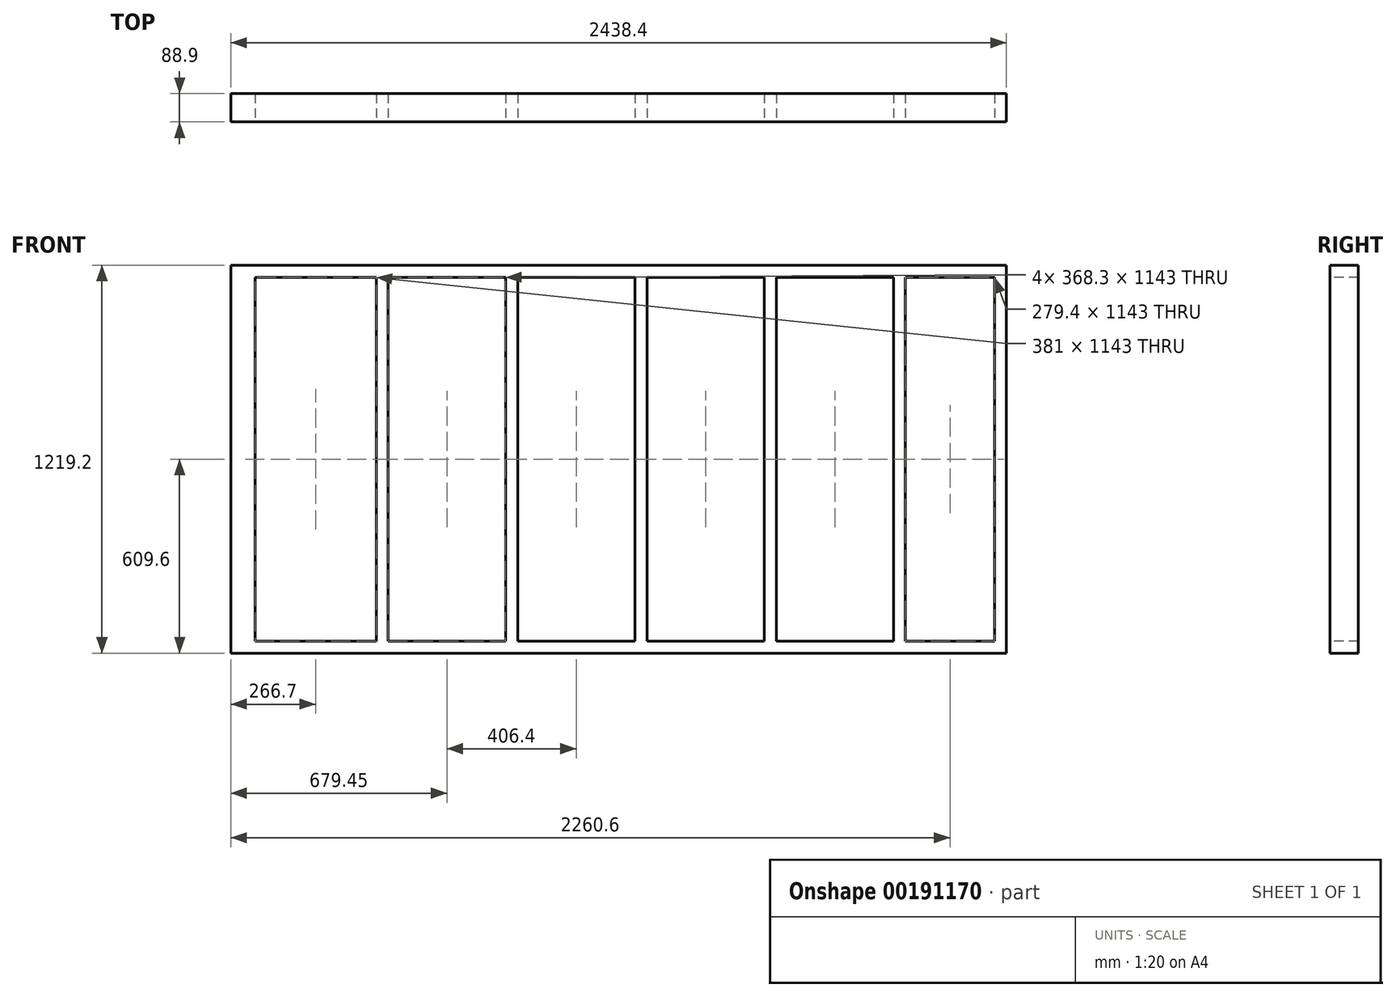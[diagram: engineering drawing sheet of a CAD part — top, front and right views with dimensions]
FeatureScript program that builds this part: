
annotation { "Feature Type Name" : "Feature", "Feature Type Description" : "" }
export const myFeature = defineFeature(function(context is Context, id is Id, definition is map)
    precondition{}
    {
        {
            var Q0;
            Q0=qCreatedBy(makeId("Top.planeOp"),FACE);
            var sketch = newSketch(context, id + "F0", { "sketchPlane" : qUnion([Q0])});
            skLineSegment(sketch, "E0.bottom", {"start": v(1219.2, -44.45) * mm, "end": v(-1219.2, -44.45) * mm});
            skLineSegment(sketch, "E0.top", {"start": v(1219.2, 44.45) * mm, "end": v(-1219.2, 44.45) * mm});
            skLineSegment(sketch, "E0.left", {"start": v(1219.2, -44.45) * mm, "end": v(1219.2, 44.45) * mm});
            skLineSegment(sketch, "E0.right", {"start": v(-1219.2, -44.45) * mm, "end": v(-1219.2, 44.45) * mm});
            skPoint(sketch, "E0.middle", {"position": v(0, 0) * mm});
            skSolve(sketch);
        }
        {
            var Q0;
            Q0 = qSketchRegion(id + "F0", true);
            extrude(context, id + "F1", {"entities" : qUnion([Q0]), "depth" : 38.1 * mm});
        }
        {
            var Q0;
            Q0=makeQuery(id+"F1.opExtrude","CAP_FACE",FACE,{"disambiguationData":[OSD([sQuery(id+"F0.wireOp",EDGE,"E0.bottom"),sQuery(id+"F0.wireOp",EDGE,"E0.top"),sQuery(id+"F0.wireOp",EDGE,"E0.left"),sQuery(id+"F0.wireOp",EDGE,"E0.right")])],"isStart":false});
            var sketch = newSketch(context, id + "F2", { "sketchPlane" : qUnion([Q0])});
            skLineSegment(sketch, "E1.bottom", {"start": v(1219.2, 44.45) * mm, "end": v(1181.1, 44.45) * mm});
            skLineSegment(sketch, "E1.top", {"start": v(1219.2, -44.45) * mm, "end": v(1181.1, -44.45) * mm});
            skLineSegment(sketch, "E1.left", {"start": v(1219.2, 44.45) * mm, "end": v(1219.2, -44.45) * mm});
            skLineSegment(sketch, "E1.right", {"start": v(1181.1, 44.45) * mm, "end": v(1181.1, -44.45) * mm});
            skLineSegment(sketch, "E2.bottom", {"start": v(901.7, 44.45) * mm, "end": v(863.6, 44.45) * mm});
            skLineSegment(sketch, "E2.top", {"start": v(901.7, -44.45) * mm, "end": v(863.6, -44.45) * mm});
            skLineSegment(sketch, "E2.left", {"start": v(901.7, 44.45) * mm, "end": v(901.7, -44.45) * mm});
            skLineSegment(sketch, "E2.right", {"start": v(863.6, 44.45) * mm, "end": v(863.6, -44.45) * mm});
            skLineSegment(sketch, "E3.bottom", {"start": v(495.3, 44.45) * mm, "end": v(457.2, 44.45) * mm});
            skLineSegment(sketch, "E3.top", {"start": v(495.3, -44.45) * mm, "end": v(457.2, -44.45) * mm});
            skLineSegment(sketch, "E3.left", {"start": v(495.3, 44.45) * mm, "end": v(495.3, -44.45) * mm});
            skLineSegment(sketch, "E3.right", {"start": v(457.2, 44.45) * mm, "end": v(457.2, -44.45) * mm});
            skLineSegment(sketch, "E4.bottom", {"start": v(88.9, 44.45) * mm, "end": v(50.8, 44.45) * mm});
            skLineSegment(sketch, "E4.top", {"start": v(88.9, -44.45) * mm, "end": v(50.8, -44.45) * mm});
            skLineSegment(sketch, "E4.left", {"start": v(88.9, 44.45) * mm, "end": v(88.9, -44.45) * mm});
            skLineSegment(sketch, "E4.right", {"start": v(50.8, 44.45) * mm, "end": v(50.8, -44.45) * mm});
            skLineSegment(sketch, "E5.bottom", {"start": v(-317.5, 44.45) * mm, "end": v(-355.6, 44.45) * mm});
            skLineSegment(sketch, "E5.top", {"start": v(-317.5, -44.45) * mm, "end": v(-355.6, -44.45) * mm});
            skLineSegment(sketch, "E5.left", {"start": v(-317.5, 44.45) * mm, "end": v(-317.5, -44.45) * mm});
            skLineSegment(sketch, "E5.right", {"start": v(-355.6, 44.45) * mm, "end": v(-355.6, -44.45) * mm});
            skLineSegment(sketch, "E6.bottom", {"start": v(-723.9, 44.45) * mm, "end": v(-762, 44.45) * mm});
            skLineSegment(sketch, "E6.top", {"start": v(-723.9, -44.45) * mm, "end": v(-762, -44.45) * mm});
            skLineSegment(sketch, "E6.left", {"start": v(-723.9, 44.45) * mm, "end": v(-723.9, -44.45) * mm});
            skLineSegment(sketch, "E6.right", {"start": v(-762, 44.45) * mm, "end": v(-762, -44.45) * mm});
            skLineSegment(sketch, "E7.bottom", {"start": v(-1219.2, 44.45) * mm, "end": v(-1181.1, 44.45) * mm});
            skLineSegment(sketch, "E7.top", {"start": v(-1219.2, -44.45) * mm, "end": v(-1181.1, -44.45) * mm});
            skLineSegment(sketch, "E7.left", {"start": v(-1219.2, 44.45) * mm, "end": v(-1219.2, -44.45) * mm});
            skLineSegment(sketch, "E7.right", {"start": v(-1181.1, 44.45) * mm, "end": v(-1181.1, -44.45) * mm});
            skLineSegment(sketch, "E8.bottom", {"start": v(-1181.1, 44.45) * mm, "end": v(-1143, 44.45) * mm});
            skLineSegment(sketch, "E8.top", {"start": v(-1181.1, -44.45) * mm, "end": v(-1143, -44.45) * mm});
            skLineSegment(sketch, "E8.right", {"start": v(-1143, 44.45) * mm, "end": v(-1143, -44.45) * mm});
            skSolve(sketch);
        }
        {
            var Q0;
            Q0 = qSketchRegion(id + "F2", true);
            extrude(context, id + "F3", {"entities" : qUnion([Q0]), "operationType" : NewBodyOperationType.ADD, "depth" : 1143 * mm});
        }
        {
            var Q0;
            Q0=makeQuery(id+"F3.boolean.opBoolean","MERGE",FACE,{"derivedFrom":[makeQuery(id+"F1.opExtrude","SWEPT_FACE",FACE,{"disambiguationData":[OSD([sQuery(id+"F0.wireOp",EDGE,"E0.bottom")])]}),makeQuery(id+"F3.opExtrude","SWEPT_FACE",FACE,{"disambiguationData":[OSD([sQuery(id+"F2.wireOp",EDGE,"E1.top")])]}),makeQuery(id+"F3.opExtrude","SWEPT_FACE",FACE,{"disambiguationData":[OSD([sQuery(id+"F2.wireOp",EDGE,"E2.top")])]}),makeQuery(id+"F3.opExtrude","SWEPT_FACE",FACE,{"disambiguationData":[OSD([sQuery(id+"F2.wireOp",EDGE,"E3.top")])]}),makeQuery(id+"F3.opExtrude","SWEPT_FACE",FACE,{"disambiguationData":[OSD([sQuery(id+"F2.wireOp",EDGE,"E4.top")])]}),makeQuery(id+"F3.opExtrude","SWEPT_FACE",FACE,{"disambiguationData":[OSD([sQuery(id+"F2.wireOp",EDGE,"E5.top")])]}),makeQuery(id+"F3.opExtrude","SWEPT_FACE",FACE,{"disambiguationData":[OSD([sQuery(id+"F2.wireOp",EDGE,"E6.top")])]}),makeQuery(id+"F3.opExtrude","SWEPT_FACE",FACE,{"disambiguationData":[OSD([sQuery(id+"F2.wireOp",EDGE,"E7.top"),sQuery(id+"F2.wireOp",EDGE,"E8.top")])]})]});
            var sketch = newSketch(context, id + "F4", { "sketchPlane" : qUnion([Q0])});
            skLineSegment(sketch, "E9.bottom", {"start": v(-1219.2, 1181.1) * mm, "end": v(1219.2, 1181.1) * mm});
            skLineSegment(sketch, "E9.top", {"start": v(-1219.2, 1219.2) * mm, "end": v(1219.2, 1219.2) * mm});
            skLineSegment(sketch, "E9.left", {"start": v(-1219.2, 1181.1) * mm, "end": v(-1219.2, 1219.2) * mm});
            skLineSegment(sketch, "E9.right", {"start": v(1219.2, 1181.1) * mm, "end": v(1219.2, 1219.2) * mm});
            skSolve(sketch);
        }
        {
            var Q0;
            Q0 = qSketchRegion(id + "F4", true);
            extrude(context, id + "F5", {"entities" : qUnion([Q0]), "operationType" : NewBodyOperationType.ADD, "oppositeDirection" : true, "depth" : 88.9 * mm});
        }
    });
